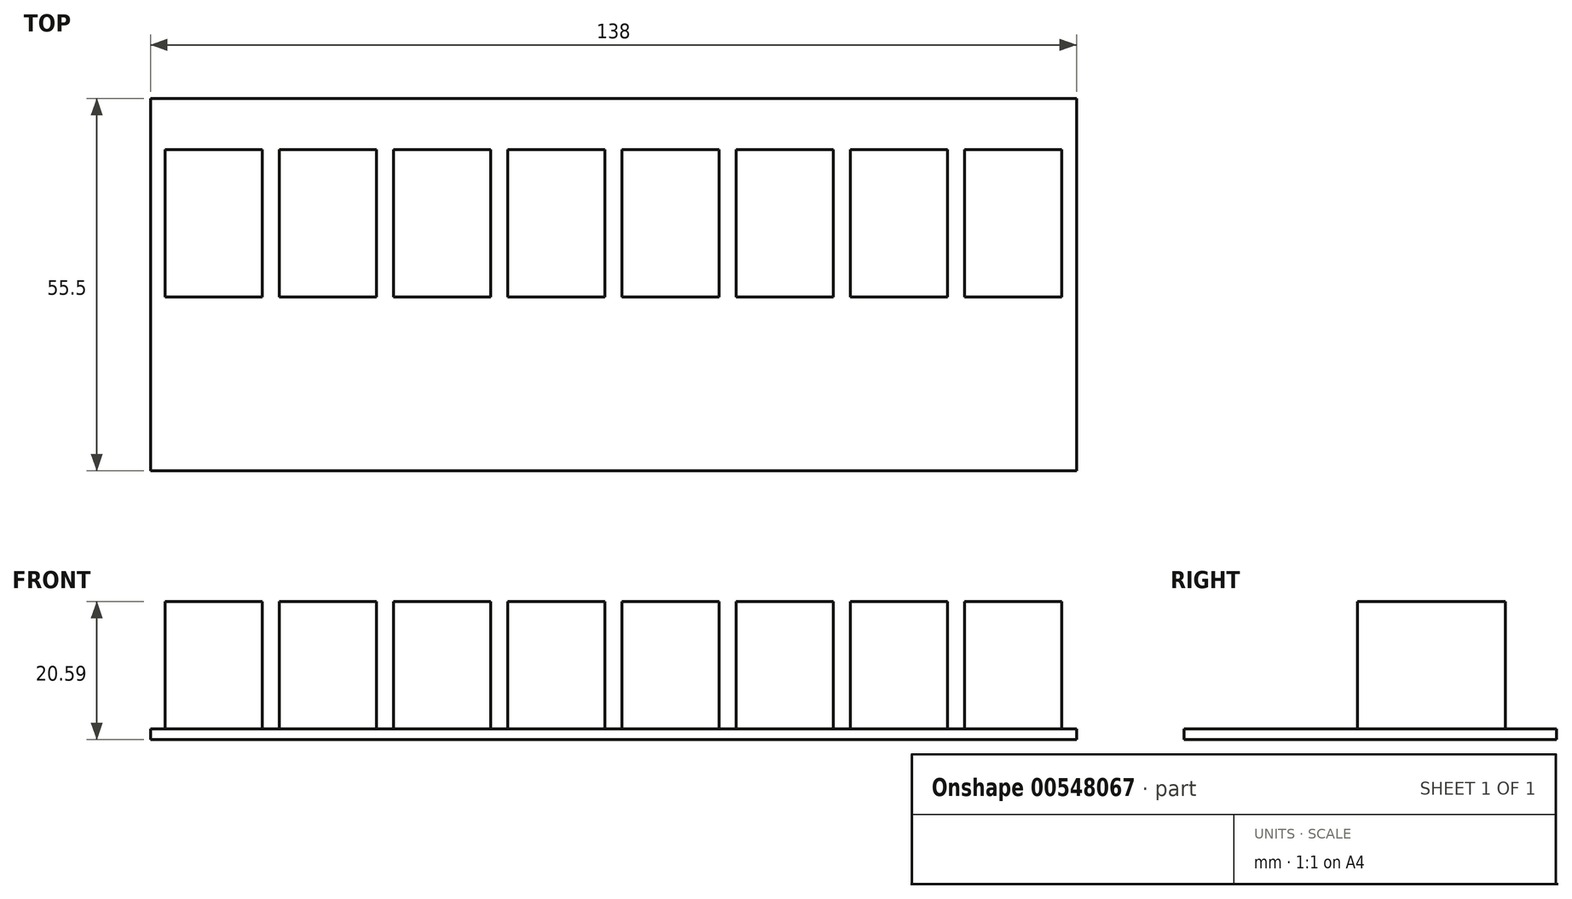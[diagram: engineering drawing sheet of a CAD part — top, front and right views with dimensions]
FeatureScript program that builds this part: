
annotation { "Feature Type Name" : "Feature", "Feature Type Description" : "" }
export const myFeature = defineFeature(function(context is Context, id is Id, definition is map)
    precondition{}
    {
        {
            var Q0;
            Q0=qCreatedBy(makeId("Top.planeOp"),FACE);
            var sketch = newSketch(context, id + "F0", { "sketchPlane" : qUnion([Q0])});
            skLineSegment(sketch, "E0.bottom", {"start": v(69, 27.75) * mm, "end": v(-69, 27.75) * mm});
            skLineSegment(sketch, "E0.top", {"start": v(69, -27.75) * mm, "end": v(-69, -27.75) * mm});
            skLineSegment(sketch, "E0.left", {"start": v(69, 27.75) * mm, "end": v(69, -27.75) * mm});
            skLineSegment(sketch, "E0.right", {"start": v(-69, 27.75) * mm, "end": v(-69, -27.75) * mm});
            skPoint(sketch, "E0.middle", {"position": v(0, 0) * mm});
            skSolve(sketch);
        }
        {
            var Q0;
            Q0 = qSketchRegion(id + "F0", true);
            var Q1;
            {var subQ0=sQuery(id+"F0.wireOp",EDGE,"I2ZxsQik-M7rb-PRnx-xZEF-tHkpyZxV4fCY");var subQ1=sQuery(id+"F0.wireOp",EDGE,"3sJrbIFc-uE7p-Sawp-S6Cc-ytHdJmApaCk6");var subQ2=makeQuery(id+"F0.imprint","INTERSECT",VERTEX,{"disambiguationData":[OD(0.0)],"derivedFrom":[subQ1,subQ0]});Q1=makeQuery(id+"F0.imprint","IMPRINT",FACE,{"disambiguationData":[TD([[makeQuery(id+"F0.imprint","IMPRINT",EDGE,{"disambiguationData":[TD([[subQ2,1.0]])],"derivedFrom":subQ1}),1.0]])]});}
            var Q2;
            {var subQ0=sQuery(id+"F0.wireOp",EDGE,"I2ZxsQik-M7rb-PRnx-xZEF-tHkpyZxV4fCY");var subQ1=sQuery(id+"F0.wireOp",EDGE,"3sJrbIFc-uE7p-Sawp-S6Cc-ytHdJmApaCk6");var subQ2=makeQuery(id+"F0.imprint","INTERSECT",VERTEX,{"disambiguationData":[OD(0.0)],"derivedFrom":[subQ1,subQ0]});Q2=makeQuery(id+"F0.imprint","IMPRINT",FACE,{"disambiguationData":[TD([[makeQuery(id+"F0.imprint","IMPRINT",EDGE,{"disambiguationData":[TD([[subQ2,-1.0]])],"derivedFrom":subQ1}),-1.0]])]});}
            var Q3;
            {var subQ0=sQuery(id+"F0.wireOp",EDGE,"I2ZxsQik-M7rb-PRnx-xZEF-tHkpyZxV4fCY");var subQ1=sQuery(id+"F0.wireOp",EDGE,"3sJrbIFc-uE7p-Sawp-S6Cc-ytHdJmApaCk6");var subQ2=makeQuery(id+"F0.imprint","INTERSECT",VERTEX,{"disambiguationData":[OD(0.0)],"derivedFrom":[subQ1,subQ0]});Q3=makeQuery(id+"F0.imprint","IMPRINT",FACE,{"disambiguationData":[TD([[makeQuery(id+"F0.imprint","IMPRINT",EDGE,{"disambiguationData":[TD([[subQ2,-1.0]])],"derivedFrom":subQ1}),1.0]])]});}
            extrude(context, id + "F1", {"entities" : qUnion([Q0, Q1, Q2, Q3]), "depth" : 1.59 * mm, "offsetDistance" : 25.4 * mm});
        }
        {
            var Q0;
            Q0=makeQuery(id+"F1.opExtrude","CAP_FACE",FACE,{"disambiguationData":[OSD([sQuery(id+"F0.wireOp",EDGE,"E0.bottom"),sQuery(id+"F0.wireOp",EDGE,"E0.top"),sQuery(id+"F0.wireOp",EDGE,"E0.left"),sQuery(id+"F0.wireOp",EDGE,"E0.right")])],"isStart":false});
            var sketch = newSketch(context, id + "F2", { "sketchPlane" : qUnion([Q0])});
            skLineSegment(sketch, "E1.bottom", {"start": v(-52.33, -1.87) * mm, "end": v(-66.8, -1.87) * mm});
            skLineSegment(sketch, "E1.top", {"start": v(-52.33, 20.13) * mm, "end": v(-66.8, 20.13) * mm});
            skLineSegment(sketch, "E1.left", {"start": v(-52.33, -1.87) * mm, "end": v(-52.33, 20.13) * mm});
            skLineSegment(sketch, "E1.right", {"start": v(-66.8, -1.87) * mm, "end": v(-66.8, 20.13) * mm});
            skPoint(sketch, "E1.middle", {"position": v(-59.56, 9.13) * mm});
            skLineSegment(sketch, "E2.1.0.0", {"start": v(-49.78, -1.87) * mm, "end": v(-49.78, 20.13) * mm});
            skLineSegment(sketch, "E2.1.0.1", {"start": v(-35.3, -1.87) * mm, "end": v(-35.3, 20.13) * mm});
            skLineSegment(sketch, "E2.1.0.2", {"start": v(-35.3, 20.13) * mm, "end": v(-49.78, 20.13) * mm});
            skLineSegment(sketch, "E2.1.0.3", {"start": v(-35.3, -1.87) * mm, "end": v(-49.78, -1.87) * mm});
            skPoint(sketch, "E2.1.0.4", {"position": v(-42.54, 9.13) * mm});
            skLineSegment(sketch, "E2.2.0.0", {"start": v(-32.76, -1.87) * mm, "end": v(-32.76, 20.13) * mm});
            skLineSegment(sketch, "E2.2.0.1", {"start": v(-18.29, -1.87) * mm, "end": v(-18.29, 20.13) * mm});
            skLineSegment(sketch, "E2.2.0.2", {"start": v(-18.29, 20.13) * mm, "end": v(-32.76, 20.13) * mm});
            skLineSegment(sketch, "E2.2.0.3", {"start": v(-18.29, -1.87) * mm, "end": v(-32.76, -1.87) * mm});
            skPoint(sketch, "E2.2.0.4", {"position": v(-25.53, 9.13) * mm});
            skLineSegment(sketch, "E2.3.0.0", {"start": v(-15.75, -1.87) * mm, "end": v(-15.75, 20.13) * mm});
            skLineSegment(sketch, "E2.3.0.1", {"start": v(-1.27, -1.87) * mm, "end": v(-1.27, 20.13) * mm});
            skLineSegment(sketch, "E2.3.0.2", {"start": v(-1.27, 20.13) * mm, "end": v(-15.75, 20.13) * mm});
            skLineSegment(sketch, "E2.3.0.3", {"start": v(-1.27, -1.87) * mm, "end": v(-15.75, -1.87) * mm});
            skPoint(sketch, "E2.3.0.4", {"position": v(-8.5, 9.13) * mm});
            skLineSegment(sketch, "E2.4.0.0", {"start": v(1.27, -1.87) * mm, "end": v(1.27, 20.13) * mm});
            skLineSegment(sketch, "E2.4.0.1", {"start": v(15.75, -1.87) * mm, "end": v(15.75, 20.13) * mm});
            skLineSegment(sketch, "E2.4.0.2", {"start": v(15.75, 20.13) * mm, "end": v(1.27, 20.13) * mm});
            skLineSegment(sketch, "E2.4.0.3", {"start": v(15.75, -1.87) * mm, "end": v(1.27, -1.87) * mm});
            skPoint(sketch, "E2.4.0.4", {"position": v(8.5, 9.13) * mm});
            skLineSegment(sketch, "E2.5.0.0", {"start": v(18.29, -1.87) * mm, "end": v(18.29, 20.13) * mm});
            skLineSegment(sketch, "E2.5.0.1", {"start": v(32.76, -1.87) * mm, "end": v(32.76, 20.13) * mm});
            skLineSegment(sketch, "E2.5.0.2", {"start": v(32.76, 20.13) * mm, "end": v(18.29, 20.13) * mm});
            skLineSegment(sketch, "E2.5.0.3", {"start": v(32.76, -1.87) * mm, "end": v(18.29, -1.87) * mm});
            skPoint(sketch, "E2.5.0.4", {"position": v(25.53, 9.13) * mm});
            skLineSegment(sketch, "E2.6.0.0", {"start": v(35.3, -1.87) * mm, "end": v(35.3, 20.13) * mm});
            skLineSegment(sketch, "E2.6.0.1", {"start": v(49.78, -1.87) * mm, "end": v(49.78, 20.13) * mm});
            skLineSegment(sketch, "E2.6.0.2", {"start": v(49.78, 20.13) * mm, "end": v(35.3, 20.13) * mm});
            skLineSegment(sketch, "E2.6.0.3", {"start": v(49.78, -1.87) * mm, "end": v(35.3, -1.87) * mm});
            skPoint(sketch, "E2.6.0.4", {"position": v(42.55, 9.13) * mm});
            skLineSegment(sketch, "E2.7.0.0", {"start": v(52.33, -1.87) * mm, "end": v(52.33, 20.13) * mm});
            skLineSegment(sketch, "E2.7.0.1", {"start": v(66.8, -1.87) * mm, "end": v(66.8, 20.13) * mm});
            skLineSegment(sketch, "E2.7.0.2", {"start": v(66.8, 20.13) * mm, "end": v(52.33, 20.13) * mm});
            skLineSegment(sketch, "E2.7.0.3", {"start": v(66.8, -1.87) * mm, "end": v(52.33, -1.87) * mm});
            skPoint(sketch, "E2.7.0.4", {"position": v(59.56, 9.13) * mm});
            skLineSegment(sketch, "E2.direction1", {"start": v(-66.8, -1.87) * mm, "end": v(-49.78, -1.87) * mm, "construction": true});
            skLineSegment(sketch, "E3", {"start": v(-66.8, 20.13) * mm, "end": v(-69, 20.13) * mm, "construction": true});
            skLineSegment(sketch, "E4", {"start": v(66.8, 20.13) * mm, "end": v(69, 20.13) * mm, "construction": true});
            skSolve(sketch);
        }
        {
            var Q0;
            Q0=makeQuery(id+"F2.imprint","IMPRINT",FACE,{"disambiguationData":[TD([[makeQuery(id+"F2.imprint","IMPRINT",EDGE,{"derivedFrom":sQuery(id+"F2.wireOp",EDGE,"E2.2.0.0")}),-1.0]])]});
            var Q1;
            Q1=makeQuery(id+"F2.imprint","IMPRINT",FACE,{"disambiguationData":[TD([[makeQuery(id+"F2.imprint","IMPRINT",EDGE,{"derivedFrom":sQuery(id+"F2.wireOp",EDGE,"E2.3.0.0")}),-1.0]])]});
            var Q2;
            Q2=makeQuery(id+"F2.imprint","IMPRINT",FACE,{"disambiguationData":[TD([[makeQuery(id+"F2.imprint","IMPRINT",EDGE,{"derivedFrom":sQuery(id+"F2.wireOp",EDGE,"E2.4.0.0")}),-1.0]])]});
            var Q3;
            Q3=makeQuery(id+"F2.imprint","IMPRINT",FACE,{"disambiguationData":[TD([[makeQuery(id+"F2.imprint","IMPRINT",EDGE,{"derivedFrom":sQuery(id+"F2.wireOp",EDGE,"E2.5.0.0")}),-1.0]])]});
            var Q4;
            Q4=makeQuery(id+"F2.imprint","IMPRINT",FACE,{"disambiguationData":[TD([[makeQuery(id+"F2.imprint","IMPRINT",EDGE,{"derivedFrom":sQuery(id+"F2.wireOp",EDGE,"E2.6.0.0")}),-1.0]])]});
            var Q5;
            Q5=makeQuery(id+"F2.imprint","IMPRINT",FACE,{"disambiguationData":[TD([[makeQuery(id+"F2.imprint","IMPRINT",EDGE,{"derivedFrom":sQuery(id+"F2.wireOp",EDGE,"E2.7.0.0")}),-1.0]])]});
            var Q6;
            Q6=makeQuery(id+"F2.imprint","IMPRINT",FACE,{"disambiguationData":[TD([[makeQuery(id+"F2.imprint","IMPRINT",EDGE,{"derivedFrom":sQuery(id+"F2.wireOp",EDGE,"E2.1.0.0")}),-1.0]])]});
            var Q7;
            Q7=makeQuery(id+"F2.imprint","IMPRINT",FACE,{"disambiguationData":[TD([[makeQuery(id+"F2.imprint","IMPRINT",EDGE,{"derivedFrom":sQuery(id+"F2.wireOp",EDGE,"E1.bottom")}),-1.0]])]});
            extrude(context, id + "F3", {"entities" : qUnion([Q0, Q1, Q2, Q3, Q4, Q5, Q6, Q7]), "operationType" : NewBodyOperationType.ADD, "depth" : 19 * mm, "offsetDistance" : 25.4 * mm});
        }
    });
